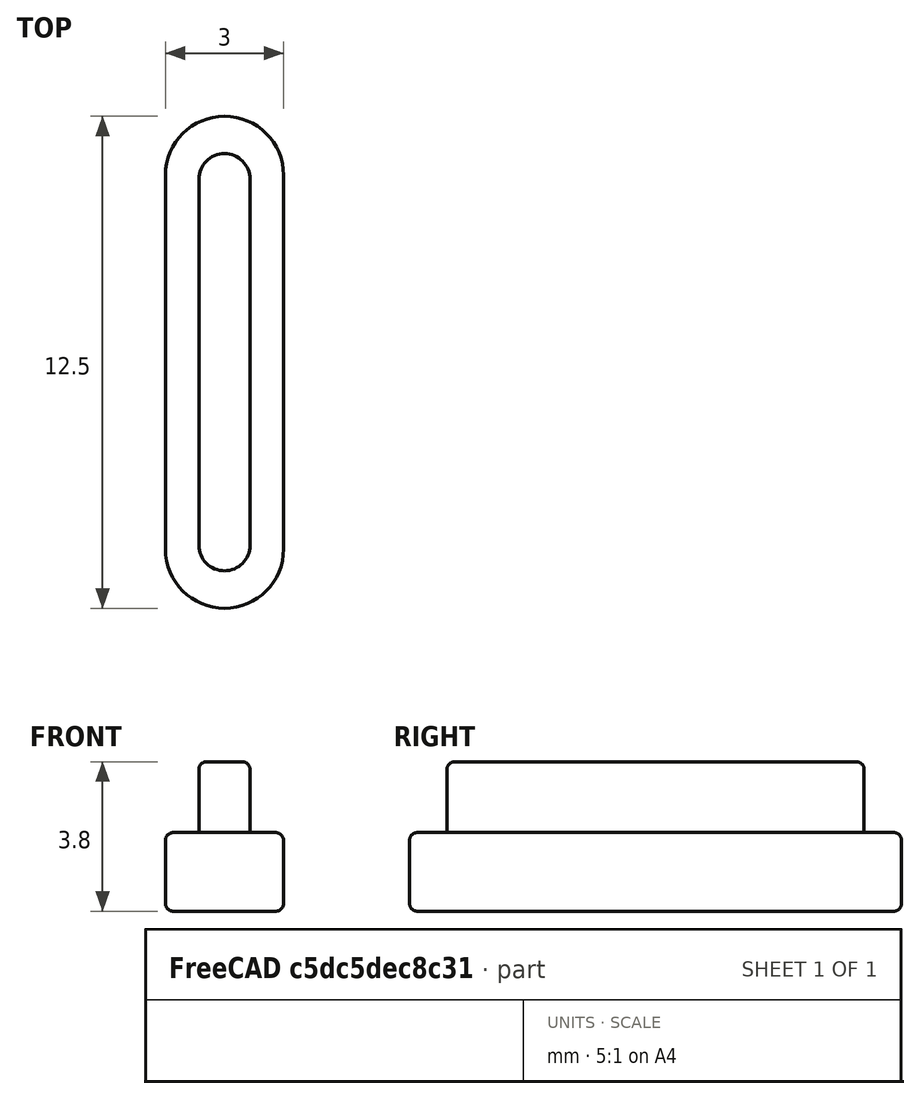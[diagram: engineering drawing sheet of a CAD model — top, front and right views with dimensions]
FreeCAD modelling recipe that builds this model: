
FCSTD DOCUMENT  (FreeCAD 0.18R13959 (Git))
Label: Light_Diffuser-PCB-v1.2
License: CreativeCommons Attribution-NonCommercial-ShareAlike
LicenseURL: http://creativecommons.org/licenses/by-nc-sa/4.0/
objects: Sketcher::SketchObject×2, PartDesign::Pad×2, PartDesign::Fillet×2, PartDesign::Body×1, Mesh::Feature×1
note: 9 computed .brp shape members not serialized (recipe doc carries the construction recipe); baked Part::Feature solids carry a one-line shape summary decoded from their .brp

FEATURE [Sketcher::SketchObject] Sketch
  MapMode = 5
  Support = -> [XY_Plane]
  sketch-geometry (8):
    g0: ArcOfCircle CenterX=0 CenterY=4.75 CenterZ=0 NormalX=0 NormalY=0 NormalZ=1 AngleXU=0 Radius=1.5 StartAngle=0 EndAngle=3.14159
    g1: ArcOfCircle CenterX=0 CenterY=-4.75 CenterZ=0 NormalX=0 NormalY=0 NormalZ=1 AngleXU=0 Radius=1.5 StartAngle=3.14159 EndAngle=6.28319
    g2: LineSegment StartX=-1.5 StartY=4.75 StartZ=0 EndX=-1.5 EndY=-4.75 EndZ=0
    g3: LineSegment StartX=1.5 StartY=4.75 StartZ=0 EndX=1.5 EndY=-4.75 EndZ=0
    g4: ArcOfCircle [constr] CenterX=0 CenterY=4.75 CenterZ=0 NormalX=0 NormalY=0 NormalZ=1 AngleXU=0 Radius=0.75 StartAngle=0 EndAngle=3.14159
    g5: ArcOfCircle [constr] CenterX=0 CenterY=-4.75 CenterZ=0 NormalX=0 NormalY=0 NormalZ=1 AngleXU=0 Radius=0.75 StartAngle=3.14159 EndAngle=6.28319
    g6: LineSegment [constr] StartX=-0.75 StartY=4.75 StartZ=0 EndX=-0.75 EndY=-4.75 EndZ=0
    g7: LineSegment [constr] StartX=0.75 StartY=4.75 StartZ=0 EndX=0.75 EndY=-4.75 EndZ=0
  constraints (20):
    c: Tangent(g0,g3) = 1.5708
    c: Tangent(g0,g2) = -1.5708
    c: Tangent(g2,g1) = -1.5708
    c: Tangent(g3,g1) = 1.5708
    c: Vertical(g2)
    c: Equal(g0,g1)
    c: PointOnObject(g0,g-2)
    c: Tangent(g4,g7) = 1.5708
    c: Tangent(g4,g6) = -1.5708
    c: Tangent(g6,g5) = -1.5708
    c: Tangent(g7,g5) = 1.5708
    c: Vertical(g6)
    c: Equal(g4,g5)
    c: PointOnObject(g4,g-2)
    c: DistanceX(g5,g5) = 1.5
    c: DistanceY(g5,g4) = 9.5
    c: DistanceX(g1,g1) = 3
    c: DistanceY(g1,g0) = 9.5
    c: Symmetric(g4,g5,g-1)
    c: Symmetric(g0,g1,g-1)
FEATURE [PartDesign::Pad] Pad
  Length = 2
  Length2 = 100
  Profile = -> Sketch
  Type = 0
FEATURE [Sketcher::SketchObject] Sketch001
  MapMode = 5
  Placement = pos=(0,0,2) rot=(0,0,1;0rad)
  Support = -> [Pad]
  sketch-geometry (4):
    g0: ArcOfCircle CenterX=0 CenterY=4.65 CenterZ=0 NormalX=0 NormalY=0 NormalZ=1 AngleXU=0 Radius=0.65 StartAngle=0 EndAngle=3.14159
    g1: ArcOfCircle CenterX=0 CenterY=-4.65 CenterZ=0 NormalX=0 NormalY=0 NormalZ=1 AngleXU=0 Radius=0.65 StartAngle=3.14159 EndAngle=6.28319
    g2: LineSegment StartX=-0.65 StartY=4.65 StartZ=0 EndX=-0.65 EndY=-4.65 EndZ=0
    g3: LineSegment StartX=0.65 StartY=4.65 StartZ=0 EndX=0.65 EndY=-4.65 EndZ=0
  constraints (10):
    c: Tangent(g0,g3) = 1.5708
    c: Tangent(g0,g2) = -1.5708
    c: Tangent(g2,g1) = -1.5708
    c: Tangent(g3,g1) = 1.5708
    c: Vertical(g2)
    c: Equal(g0,g1)
    c: PointOnObject(g0,g-2)
    c: DistanceY(g1,g0) = 9.3
    c: DistanceX(g1,g1) = 1.3
    c: Symmetric(g0,g1,g-1)
FEATURE [PartDesign::Pad] Pad001
  BaseFeature = -> Pad
  Length = 1.8
  Length2 = 100
  Profile = -> Sketch001
  Type = 0
FEATURE [PartDesign::Fillet] Fillet
  Base = -> Pad001 [Edge24]
  BaseFeature = -> Pad001
  Radius = 0.2
FEATURE [PartDesign::Fillet] Fillet001
  Base = -> Fillet [Edge12,Edge29]
  BaseFeature = -> Fillet
  Radius = 0.2
FEATURE [PartDesign::Body] Body
  Group = -> [Sketch,Pad,Sketch001,Pad001,Fillet,Fillet001]
  Origin = -> Origin
  Tip = -> Fillet001
FEATURE [Mesh::Feature] Mesh  label="Fillet001 (Meshed)"
